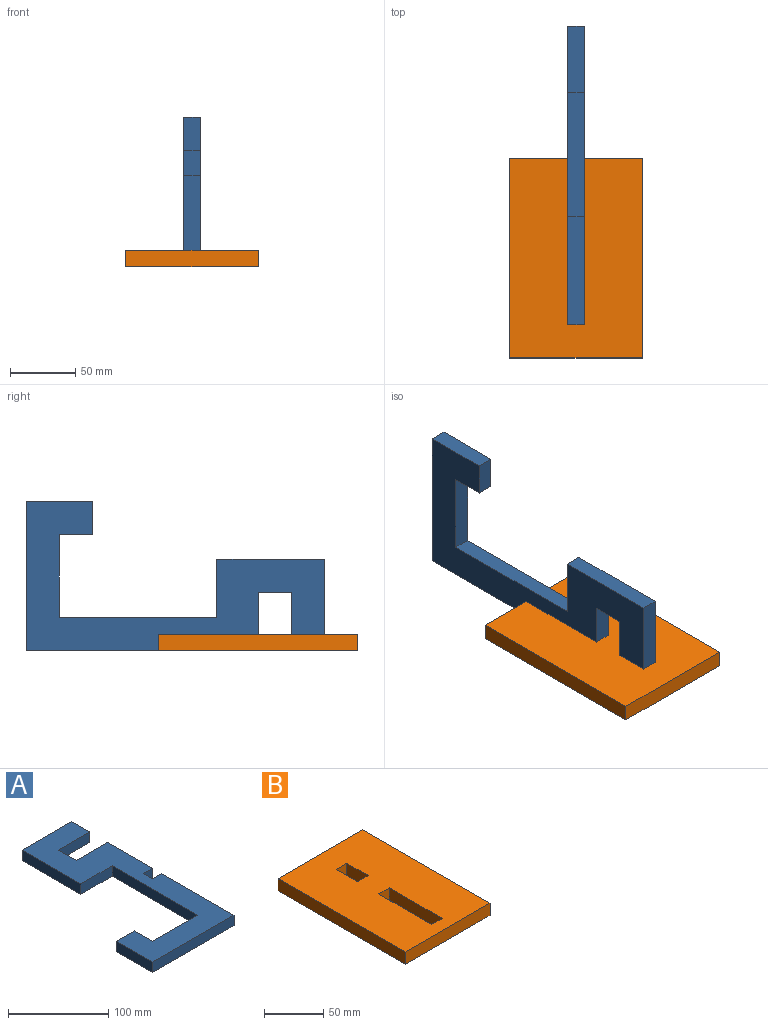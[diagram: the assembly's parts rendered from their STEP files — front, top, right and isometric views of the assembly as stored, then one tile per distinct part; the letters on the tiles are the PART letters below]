
ASSEMBLY  parts=2 mates=1
PART A: 20 faces, bbox 114.3x228.6x12.7 mm
  f0: plane 101.6x12.7mm, normal (1,0,0), area 1290.3mm2, adj f1,f17,f18,f19
  f1: plane 12.7x12.7mm, normal (0,1,0), area 161.3mm2, adj f0,f2,f18,f19
  f2: plane 12.7x12.7mm, normal (1,0,0), area 161.3mm2, adj f1,f3,f18,f19
  f3: plane 12.7x12.7mm, normal (0,-1,0), area 161.3mm2, adj f2,f4,f18,f19
  f4: plane 63.5x12.7mm, normal (1,0,0), area 806.5mm2, adj f3,f5,f18,f19
  f5: plane 44.45x12.7mm, normal (0,1,0), area 564.5mm2, adj f4,f6,f18,f19
  f6: plane 25.4x12.7mm, normal (1,0,0), area 322.6mm2, adj f5,f7,f18,f19
  f7: plane 44.45x12.7mm, normal (0,-1,0), area 564.5mm2, adj f6,f8,f18,f19
  f8: plane 25.4x12.7mm, normal (1,0,0), area 322.6mm2, adj f7,f9,f18,f19
  f9: plane 69.85x12.7mm, normal (0,1,0), area 887.1mm2, adj f8,f10,f18,f19
  f10: plane 82.55x12.7mm, normal (-1,0,0), area 1048.4mm2, adj f9,f11,f18,f19
  f11: plane 44.45x12.7mm, normal (0,-1,0), area 564.5mm2, adj f10,f12,f18,f19
  f12: plane 120.65x12.7mm, normal (-1,0,0), area 1532.3mm2, adj f11,f13,f18,f19
  f13: plane 63.5x12.7mm, normal (0,1,0), area 806.4mm2, adj f12,f14,f18,f19
  f14: plane 25.4x12.7mm, normal (1,0,0), area 322.6mm2, adj f13,f15,f18,f19
  f15: plane 25.4x12.7mm, normal (0,1,0), area 322.6mm2, adj f14,f16,f18,f19
  f16: plane 50.8x12.7mm, normal (-1,0,0), area 645.2mm2, adj f15,f17,f18,f19
  f17: plane 114.3x12.7mm, normal (0,-1,0), area 1451.6mm2, adj f0,f16,f18,f19
  f18: plane 228.6x114.3mm, normal (0,0,1), area 11088.7mm2, adj f0,f1,f2,f3,f4,f5,f6,f7
  f19: plane 228.6x114.3mm, normal (0,0,-1), area 11088.7mm2, adj f0,f1,f2,f3,f4,f5,f6,f7
PART B: 14 faces, bbox 101.6x152.4x12.7 mm
  f0: plane 101.6x12.7mm, normal (0,1,0), area 1290.3mm2, adj f1,f11,f12,f13
  f1: plane 152.4x12.7mm, normal (-1,0,0), area 1935.5mm2, adj f0,f2,f12,f13
  f2: plane 101.6x12.7mm, normal (0,-1,0), area 1290.3mm2, adj f1,f11,f12,f13
  f3: plane 12.7x12.7mm, normal (0,-1,0), area 161.3mm2, adj f4,f9,f12,f13
  f4: plane 25.4x12.7mm, normal (-1,0,0), area 322.6mm2, adj f3,f5,f12,f13
  f5: plane 12.7x12.7mm, normal (0,1,0), area 161.3mm2, adj f4,f9,f12,f13
  f6: plane 12.7x12.7mm, normal (0,-1,0), area 161.3mm2, adj f7,f10,f12,f13
  f7: plane 63.5x12.7mm, normal (-1,0,0), area 806.5mm2, adj f6,f8,f12,f13
  f8: plane 12.7x12.7mm, normal (0,1,0), area 161.3mm2, adj f7,f10,f12,f13
  f9: plane 25.4x12.7mm, normal (1,0,0), area 322.6mm2, adj f3,f5,f12,f13
  f10: plane 63.5x12.7mm, normal (1,0,0), area 806.5mm2, adj f6,f8,f12,f13
  f11: plane 152.4x12.7mm, normal (1,0,0), area 1935.5mm2, adj f0,f2,f12,f13
  f12: plane 152.4x101.6mm, normal (0,0,1), area 14354.8mm2, adj f0,f1,f2,f3,f4,f5,f6,f7
  f13: plane 152.4x101.6mm, normal (0,0,-1), area 14354.8mm2, adj f0,f1,f2,f3,f4,f5,f6,f7
PLACE A rot(axis=(0.71,0,-0.71),180deg) t=(41.78,48.18,-125.29)mm
PLACE B rot(axis=(1,0,0),180deg) t=(-52.93,154.14,-45.07)mm
MATE fastened A.f8 <-> B.f12  axis (0,0,-1) through (29.08,-101.73,-57.77)mm
